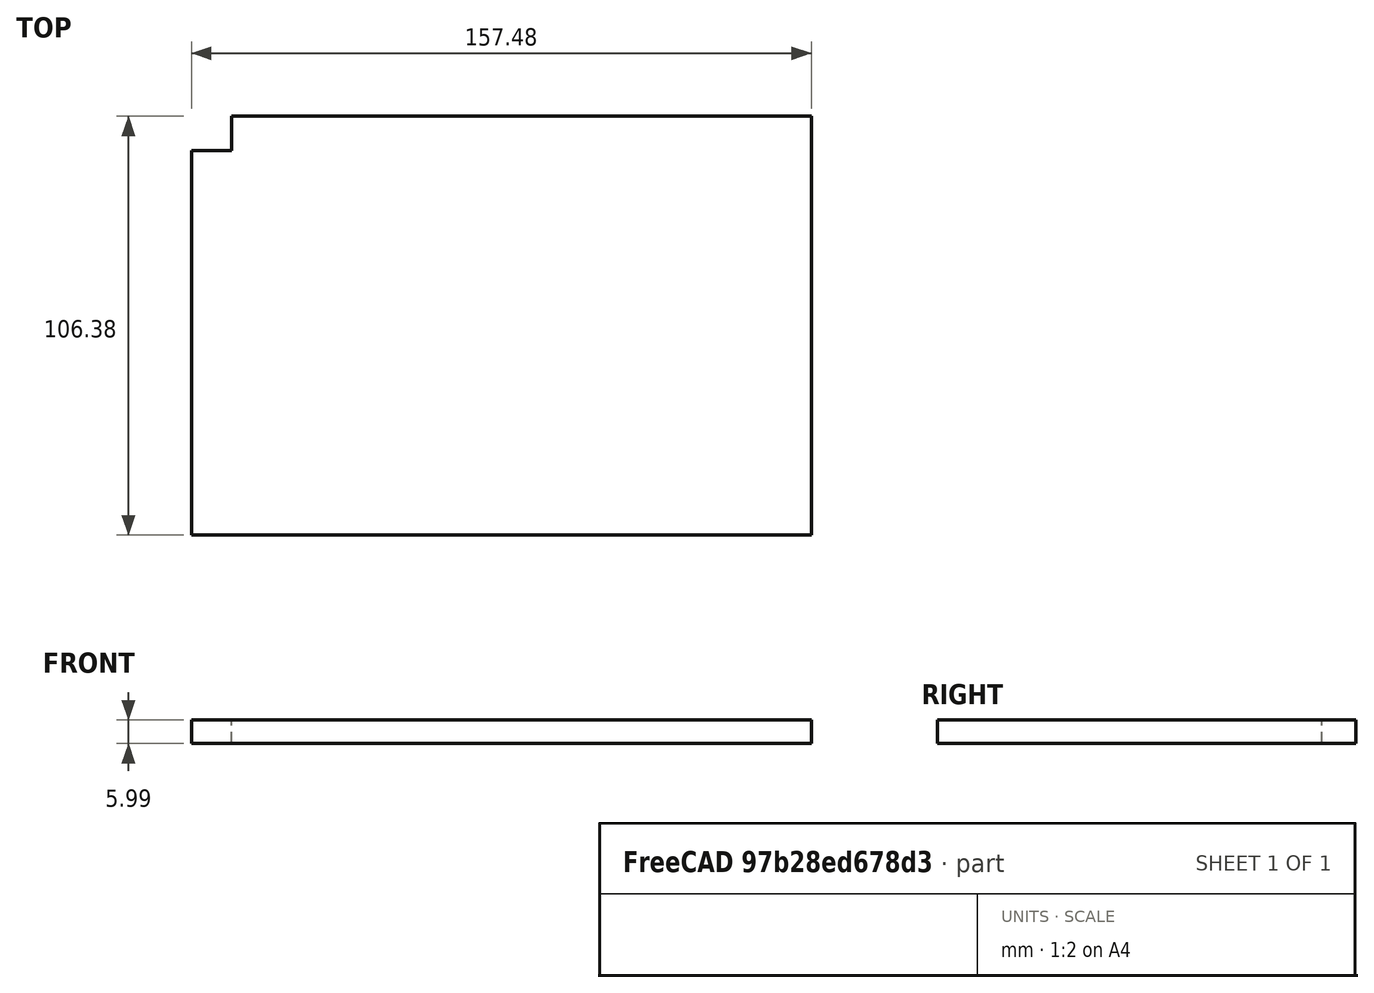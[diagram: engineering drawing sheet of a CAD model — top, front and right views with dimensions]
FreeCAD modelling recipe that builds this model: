
FCSTD DOCUMENT  (FreeCAD 0.19R24267 (Git))
Label: Inv1-P16
License: All rights reserved
LicenseURL: http://en.wikipedia.org/wiki/All_rights_reserved
objects: TechDraw::DrawViewDimension×5, TechDraw::DrawProjGroupItem×2, TechDraw::DrawHatch×2, TechDraw::DrawViewAnnotation×2, Sketcher::SketchObject×1, Part::Extrusion×1, TechDraw::DrawSVGTemplate×1, TechDraw::DrawProjGroup×1, TechDraw::DrawPage×1
note: 2 computed .brp shape members not serialized (recipe doc carries the construction recipe); baked Part::Feature solids carry a one-line shape summary decoded from their .brp

FEATURE [Sketcher::SketchObject] Sketch
  FullyConstrained = false
  sketch-geometry (8):
    g0: LineSegment StartX=-55.9107 StartY=-85.906 StartZ=0 EndX=101.569 EndY=-85.906 EndZ=0
    g1: LineSegment StartX=101.569 StartY=-85.906 StartZ=0 EndX=101.569 EndY=20.4692 EndZ=0
    g2: LineSegment StartX=-55.9107 StartY=-85.906 StartZ=0 EndX=-55.9107 EndY=11.757 EndZ=0
    g3: LineSegment StartX=101.569 StartY=20.4692 StartZ=0 EndX=-45.6745 EndY=20.4692 EndZ=0
    g4: LineSegment StartX=-55.9107 StartY=11.757 StartZ=0 EndX=-45.6745 EndY=11.757 EndZ=0
    g5: LineSegment StartX=-45.6745 StartY=11.757 StartZ=0 EndX=-45.6745 EndY=20.4692 EndZ=0
    g6: LineSegment StartX=-55.9107 StartY=11.757 StartZ=0 EndX=-45.6745 EndY=11.757 EndZ=0
    g7: LineSegment StartX=-55.9107 StartY=11.757 StartZ=0 EndX=-45.6745 EndY=11.757 EndZ=0
  constraints (24):
    c: Horizontal(g0)
    c: DistanceX(g0,g0) = 157.48
    c: Coincident(g1,g0)
    c: Vertical(g1)
    c: DistanceY(g1,g1) = 106.375
    c: Coincident(g2,g0)
    c: Vertical(g2)
    c: DistanceY(g2,g2) = 97.663
    c: Coincident(g3,g1)
    c: Horizontal(g3)
    c: Coincident(g4,g2)
    c: Horizontal(g4)
    c: DistanceX(g4,g4) = 10.2362
    c: Coincident(g5,g4)
    c: Coincident(g5,g3)
    c: Equal(g2,g1)
    c: Equal(g0,g3)
    c: Equal(g4,g0)
    c: Equal(g5,g1)
    c: Coincident(g6,g2)
    c: Coincident(g6,g4)
    c: Coincident(g7,g2)
    c: Coincident(g7,g4)
    c: Horizontal(g7)
FEATURE [Part::Extrusion] Extrude
  Base = -> Sketch
  Dir = (0,0,1)
  DirMode = 2
  FaceMakerClass = Part::FaceMakerBullseye
  LengthFwd = 5.9944
  LengthRev = 0
  Solid = true
  Symmetric = false
FEATURE [TechDraw::DrawSVGTemplate] Template
  Height = 215.9
  Orientation = 1
  Width = 279.4
FEATURE [TechDraw::DrawProjGroupItem] ProjItem  label="Front"
  CoarseView = false
  Direction = (0,0,1)
  Focus = 100
  HardHidden = false
  IsoCount = 0
  IsoHidden = false
  IsoVisible = false
  LockPosition = true
  Perspective = false
  Rotation = 0
  RotationVector = (1,0,0)
  Scale = 0.5
  ScaleType = 2
  SeamHidden = false
  SeamVisible = true
  SmoothHidden = false
  SmoothVisible = true
  Source = -> [Extrude]
  Type = 0
  X = 0
  XDirection = (1,0,0)
  Y = 0
FEATURE [TechDraw::DrawProjGroupItem] ProjItem001  label="Left"
  CoarseView = false
  Direction = (-1,0,1e-16)
  Focus = 100
  HardHidden = false
  IsoCount = 0
  IsoHidden = false
  IsoVisible = false
  LockPosition = false
  Perspective = false
  Rotation = 0
  RotationVector = (1,0,0)
  Scale = 0.5
  ScaleType = 2
  SeamHidden = false
  SeamVisible = true
  SmoothHidden = false
  SmoothVisible = true
  Source = -> [Extrude]
  Type = 1
  X = 79.2735
  XDirection = (1e-16,0,1)
  Y = 0
FEATURE [TechDraw::DrawProjGroup] ProjGroup
  Anchor = -> ProjItem
  AutoDistribute = true
  LockPosition = false
  ProjectionType = 0
  Rotation = 0
  Scale = 0.5
  ScaleType = 2
  Source = -> [Extrude]
  Views = -> [ProjItem,ProjItem001]
  X = 120.28
  Y = 100.446
  spacingX = 15.0114
  spacingY = 15.0114
FEATURE [TechDraw::DrawHatch] Hatch  label="HatchF0"
  HatchPattern = <path>
  Source = -> ProjItem [Face0]
FEATURE [TechDraw::DrawHatch] Hatch001  label="Hatch001F1"
  HatchPattern = <path>
  Source = -> ProjItem001 [Face1,Face2]
FEATURE [TechDraw::DrawViewDimension] Dimension
  Arbitrary = false
  ArbitraryTolerances = false
  EqualTolerance = true
  FormatSpec = %.3f
  FormatSpecOverTolerance = %+.3f
  FormatSpecUnderTolerance = %+.3f
  Inverted = false
  LockPosition = false
  MeasureType = 1
  OverTolerance = 0
  References2D = -> [ProjItem]
  Rotation = 0
  ScaleType = 0
  TheoreticalExact = false
  Type = 1
  UnderTolerance = 0
  X = -0.335756
  Y = -41.3671
FEATURE [TechDraw::DrawViewDimension] Dimension001
  Arbitrary = false
  ArbitraryTolerances = false
  EqualTolerance = true
  FormatSpec = %.3f
  FormatSpecOverTolerance = %+.3f
  FormatSpecUnderTolerance = %+.3f
  Inverted = false
  LockPosition = false
  MeasureType = 1
  OverTolerance = 0
  References2D = -> [ProjItem]
  Rotation = 0
  ScaleType = 0
  TheoreticalExact = false
  Type = 2
  UnderTolerance = 0
  X = 47.5307
  Y = 0.466328
FEATURE [TechDraw::DrawViewDimension] Dimension002
  Arbitrary = false
  ArbitraryTolerances = false
  EqualTolerance = true
  FormatSpec = %.3f
  FormatSpecOverTolerance = %+.3f
  FormatSpecUnderTolerance = %+.3f
  Inverted = false
  LockPosition = false
  MeasureType = 1
  OverTolerance = 0
  References2D = -> [ProjItem]
  Rotation = 0
  ScaleType = 0
  TheoreticalExact = false
  Type = 1
  UnderTolerance = 0
  X = -58.832
  Y = 9.44607
FEATURE [TechDraw::DrawViewDimension] Dimension003
  Arbitrary = false
  ArbitraryTolerances = false
  EqualTolerance = true
  FormatSpec = %.3f
  FormatSpecOverTolerance = %+.3f
  FormatSpecUnderTolerance = %+.3f
  Inverted = false
  LockPosition = false
  MeasureType = 1
  OverTolerance = 0
  References2D = -> [ProjItem]
  Rotation = 0
  ScaleType = 0
  TheoreticalExact = false
  Type = 2
  UnderTolerance = 0
  X = -27.2279
  Y = 45.7006
FEATURE [TechDraw::DrawViewDimension] Dimension004
  Arbitrary = false
  ArbitraryTolerances = false
  EqualTolerance = true
  FormatSpec = %.3f
  FormatSpecOverTolerance = %+.3f
  FormatSpecUnderTolerance = %+.3f
  Inverted = false
  LockPosition = false
  MeasureType = 1
  OverTolerance = 0
  References2D = -> [ProjItem001]
  Rotation = 0
  ScaleType = 0
  TheoreticalExact = false
  Type = 1
  UnderTolerance = 0
  X = 22.4674
  Y = 12.2561
FEATURE [TechDraw::DrawViewAnnotation] Annotation
  Font = osifont
  LineSpace = 80
  LockPosition = false
  MaxWidth = -1
  Rotation = 0
  ScaleType = 0
  Text = Figure S1 (Inverted 1) | Panel 16 [focus knob top left] | Quantity: 1
  TextSize = 5.0038
  TextStyle = 0
  X = 42.148
  Y = 195.58
FEATURE [TechDraw::DrawViewAnnotation] Annotation002
  Font = osifont
  LineSpace = 80
  LockPosition = false
  MaxWidth = -1
  Rotation = 0
  ScaleType = 0
  Text = Units: Inches
  TextSize = 5.0038
  TextStyle = 0
  X = 259.08
  Y = 5.08
FEATURE [TechDraw::DrawPage] Page
  KeepUpdated = true
  NextBalloonIndex = 1
  ProjectionType = 0
  Template = -> Template
  Views = -> [ProjGroup,Dimension,Dimension001,Dimension002,Dimension003,Dimension004,Annotation,Annotation002]
note: 2 file-system paths scrubbed to <path> (originals preserved in the JSON sidecar)
